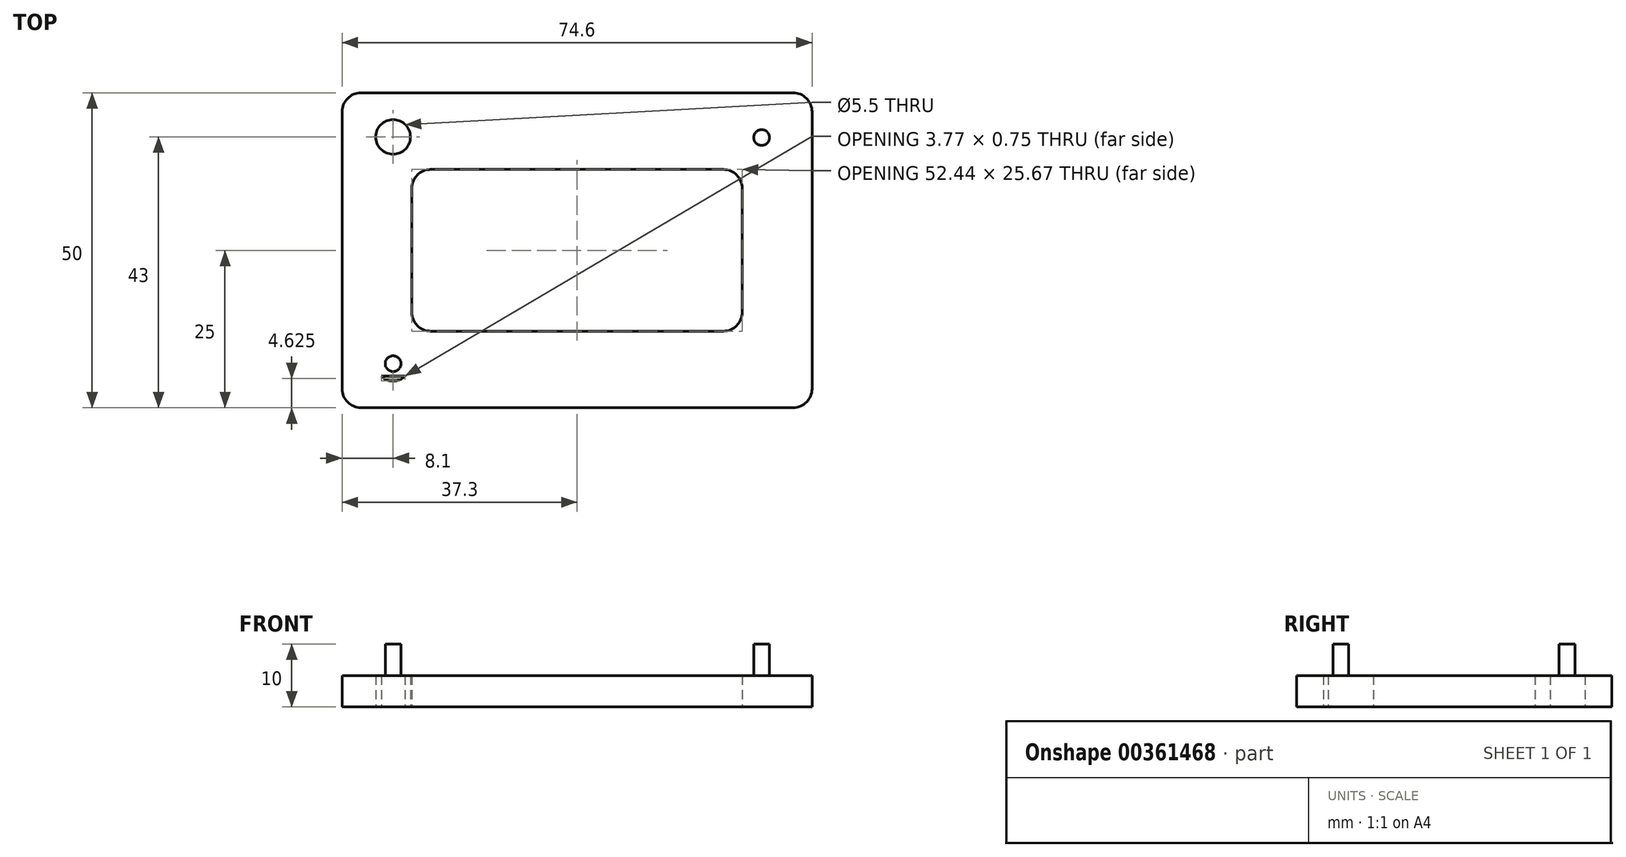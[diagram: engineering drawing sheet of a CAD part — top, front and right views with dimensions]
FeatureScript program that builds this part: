
annotation { "Feature Type Name" : "Feature", "Feature Type Description" : "" }
export const myFeature = defineFeature(function(context is Context, id is Id, definition is map)
    precondition{}
    {
        {
            var Q0;
            Q0=qCreatedBy(makeId("Top.planeOp"),FACE);
            var sketch = newSketch(context, id + "F0", { "sketchPlane" : qUnion([Q0])});
            skLineSegment(sketch, "E0.bottom", {"start": v(-32.3, 20) * mm, "end": v(32.3, 20) * mm});
            skLineSegment(sketch, "E0.top", {"start": v(-32.3, -20) * mm, "end": v(32.3, -20) * mm});
            skLineSegment(sketch, "E0.left", {"start": v(-32.3, 20) * mm, "end": v(-32.3, -20) * mm});
            skLineSegment(sketch, "E0.right", {"start": v(32.3, 20) * mm, "end": v(32.3, -20) * mm});
            skPoint(sketch, "E0.middle", {"position": v(0, 0) * mm});
            skCircle(sketch, "E1", {"center": v(29.3, 17.9) * mm, "radius": 1.25 * mm});
            skCircle(sketch, "E2", {"center": v(-29.2, -18) * mm, "radius": 1.25 * mm});
            skLineSegment(sketch, "E3.0", {"start": v(-37.3, 25) * mm, "end": v(37.3, 25) * mm});
            skLineSegment(sketch, "E3.1", {"start": v(-37.3, 25) * mm, "end": v(-37.3, -25) * mm});
            skLineSegment(sketch, "E3.2", {"start": v(-37.3, -25) * mm, "end": v(37.3, -25) * mm});
            skLineSegment(sketch, "E3.3", {"start": v(37.3, 25) * mm, "end": v(37.3, -25) * mm});
            skCircle(sketch, "E4.0", {"center": v(29.3, 17.9) * mm, "radius": 2.75 * mm});
            skCircle(sketch, "E5.0", {"center": v(-29.2, -18) * mm, "radius": 2.75 * mm});
            skLineSegment(sketch, "E6.bottom", {"start": v(-26.22, 12.84) * mm, "end": v(26.22, 12.84) * mm});
            skLineSegment(sketch, "E6.top", {"start": v(-26.22, -12.84) * mm, "end": v(26.22, -12.84) * mm});
            skLineSegment(sketch, "E6.left", {"start": v(-26.22, 12.84) * mm, "end": v(-26.22, -12.84) * mm});
            skLineSegment(sketch, "E6.right", {"start": v(26.22, 12.84) * mm, "end": v(26.22, -12.84) * mm});
            skCircle(sketch, "E7.MirrorC", {"center": v(-29.2, 18) * mm, "radius": 2.75 * mm});
            skCircle(sketch, "E8.MirrorC", {"center": v(29.3, -17.9) * mm, "radius": 2.75 * mm});
            skSolve(sketch);
        }
        {
            var Q0;
            Q0=makeQuery(id+"F0.imprint","IMPRINT",FACE,{"disambiguationData":[TD([[makeQuery(id+"F0.imprint","IMPRINT",EDGE,{"derivedFrom":sQuery(id+"F0.wireOp",EDGE,"E0.bottom")}),1.0]])]});
            var Q1;
            Q1=makeQuery(id+"F0.imprint","IMPRINT",FACE,{"disambiguationData":[TD([[makeQuery(id+"F0.imprint","IMPRINT",EDGE,{"derivedFrom":sQuery(id+"F0.wireOp",EDGE,"E0.bottom")}),-1.0]])]});
            var Q2;
            Q2=makeQuery(id+"F0.imprint","IMPRINT",FACE,{"disambiguationData":[TD([[makeQuery(id+"F0.imprint","IMPRINT",EDGE,{"derivedFrom":sQuery(id+"F0.wireOp",EDGE,"E2")}),1.0]])]});
            var Q3;
            Q3=makeQuery(id+"F0.imprint","IMPRINT",FACE,{"disambiguationData":[TD([[makeQuery(id+"F0.imprint","IMPRINT",EDGE,{"derivedFrom":sQuery(id+"F0.wireOp",EDGE,"E1")}),1.0]])]});
            var Q4;
            Q4=makeQuery(id+"F0.imprint","IMPRINT",FACE,{"disambiguationData":[TD([[makeQuery(id+"F0.imprint","IMPRINT",EDGE,{"derivedFrom":sQuery(id+"F0.wireOp",EDGE,"E1")}),-1.0]])]});
            var Q5;
            Q5=makeQuery(id+"F0.imprint","IMPRINT",FACE,{"disambiguationData":[TD([[makeQuery(id+"F0.imprint","IMPRINT",EDGE,{"derivedFrom":sQuery(id+"F0.wireOp",EDGE,"E2")}),-1.0]])]});
            var Q6;
            {var subQ1=sQuery(id+"F0.wireOp",EDGE,"E0.left");Q6=makeQuery(id+"F0.imprint","IMPRINT",FACE,{"disambiguationData":[TD([[makeQuery(id+"F0.imprint","IMPRINT",EDGE,{"derivedFrom":subQ1}),-1.0]])]});}
            var Q7;
            {var subQ0=sQuery(id+"F0.wireOp",EDGE,"E5.0");var subQ1=sQuery(id+"F0.wireOp",EDGE,"E0.top");var subQ2=makeQuery(id+"F0.imprint","INTERSECT",VERTEX,{"disambiguationData":[OD(0.0)],"derivedFrom":[subQ1,subQ0]});Q7=makeQuery(id+"F0.imprint","IMPRINT",FACE,{"disambiguationData":[TD([[makeQuery(id+"F0.imprint","IMPRINT",EDGE,{"disambiguationData":[TD([[subQ2,-1.0]])],"derivedFrom":subQ1}),-1.0]])]});}
            extrude(context, id + "F1", {"entities" : qUnion([Q0, Q1, Q2, Q3, Q4, Q5, Q6, Q7]), "depth" : 2 * mm});
        }
        {
            var Q0;
            {var subQ0=sQuery(id+"F0.wireOp",EDGE,"E4.0");var subQ1=sQuery(id+"F0.wireOp",EDGE,"E0.bottom");var subQ2=makeQuery(id+"F0.imprint","INTERSECT",VERTEX,{"disambiguationData":[OD(0.0)],"derivedFrom":[subQ1,subQ0]});Q0=makeQuery(id+"F0.imprint","IMPRINT",FACE,{"disambiguationData":[TD([[makeQuery(id+"F0.imprint","IMPRINT",EDGE,{"disambiguationData":[TD([[subQ2,-1.0]])],"derivedFrom":subQ1}),1.0]])]});}
            var Q1;
            Q1=makeQuery(id+"F0.imprint","IMPRINT",FACE,{"disambiguationData":[TD([[makeQuery(id+"F0.imprint","IMPRINT",EDGE,{"derivedFrom":sQuery(id+"F0.wireOp",EDGE,"E1")}),-1.0]])]});
            var Q2;
            Q2=makeQuery(id+"F0.imprint","IMPRINT",FACE,{"disambiguationData":[TD([[makeQuery(id+"F0.imprint","IMPRINT",EDGE,{"derivedFrom":sQuery(id+"F0.wireOp",EDGE,"E1")}),1.0]])]});
            var Q3;
            Q3=makeQuery(id+"F0.imprint","IMPRINT",FACE,{"disambiguationData":[TD([[makeQuery(id+"F0.imprint","IMPRINT",EDGE,{"derivedFrom":sQuery(id+"F0.wireOp",EDGE,"E2")}),-1.0]])]});
            var Q4;
            Q4=makeQuery(id+"F0.imprint","IMPRINT",FACE,{"disambiguationData":[TD([[makeQuery(id+"F0.imprint","IMPRINT",EDGE,{"derivedFrom":sQuery(id+"F0.wireOp",EDGE,"E2")}),1.0]])]});
            var Q5;
            {var subQ0=sQuery(id+"F0.wireOp",EDGE,"E5.0");var subQ1=sQuery(id+"F0.wireOp",EDGE,"E0.top");var subQ2=makeQuery(id+"F0.imprint","INTERSECT",VERTEX,{"disambiguationData":[OD(0.0)],"derivedFrom":[subQ1,subQ0]});Q5=makeQuery(id+"F0.imprint","IMPRINT",FACE,{"disambiguationData":[TD([[makeQuery(id+"F0.imprint","IMPRINT",EDGE,{"disambiguationData":[TD([[subQ2,-1.0]])],"derivedFrom":subQ1}),-1.0]])]});}
            var Q6;
            {var subQ0=sQuery(id+"F0.wireOp",EDGE,"E7.MirrorC");var subQ1=sQuery(id+"F0.wireOp",EDGE,"E0.bottom");var subQ2=makeQuery(id+"F0.imprint","INTERSECT",VERTEX,{"disambiguationData":[OD(0.0)],"derivedFrom":[subQ1,subQ0]});Q6=makeQuery(id+"F0.imprint","IMPRINT",FACE,{"disambiguationData":[TD([[makeQuery(id+"F0.imprint","IMPRINT",EDGE,{"disambiguationData":[TD([[subQ2,-1.0]])],"derivedFrom":subQ1}),-1.0]])]});}
            var Q7;
            {var subQ0=sQuery(id+"F0.wireOp",EDGE,"E7.MirrorC");var subQ1=sQuery(id+"F0.wireOp",EDGE,"E0.bottom");var subQ2=makeQuery(id+"F0.imprint","INTERSECT",VERTEX,{"disambiguationData":[OD(0.0)],"derivedFrom":[subQ1,subQ0]});Q7=makeQuery(id+"F0.imprint","IMPRINT",FACE,{"disambiguationData":[TD([[makeQuery(id+"F0.imprint","IMPRINT",EDGE,{"disambiguationData":[TD([[subQ2,-1.0]])],"derivedFrom":subQ1}),1.0]])]});}
            var Q8;
            {var subQ0=sQuery(id+"F0.wireOp",EDGE,"E8.MirrorC");var subQ1=sQuery(id+"F0.wireOp",EDGE,"E0.top");var subQ2=makeQuery(id+"F0.imprint","INTERSECT",VERTEX,{"disambiguationData":[OD(0.0)],"derivedFrom":[subQ1,subQ0]});Q8=makeQuery(id+"F0.imprint","IMPRINT",FACE,{"disambiguationData":[TD([[makeQuery(id+"F0.imprint","IMPRINT",EDGE,{"disambiguationData":[TD([[subQ2,-1.0]])],"derivedFrom":subQ1}),1.0]])]});}
            var Q9;
            {var subQ0=sQuery(id+"F0.wireOp",EDGE,"E8.MirrorC");var subQ1=sQuery(id+"F0.wireOp",EDGE,"E0.top");var subQ2=makeQuery(id+"F0.imprint","INTERSECT",VERTEX,{"disambiguationData":[OD(0.0)],"derivedFrom":[subQ1,subQ0]});Q9=makeQuery(id+"F0.imprint","IMPRINT",FACE,{"disambiguationData":[TD([[makeQuery(id+"F0.imprint","IMPRINT",EDGE,{"disambiguationData":[TD([[subQ2,-1.0]])],"derivedFrom":subQ1}),-1.0]])]});}
            extrude(context, id + "F2", {"entities" : qUnion([Q0, Q1, Q2, Q3, Q4, Q5, Q6, Q7, Q8, Q9]), "operationType" : NewBodyOperationType.ADD, "depth" : 5 * mm});
        }
        {
            var Q0;
            Q0=makeQuery(id+"F0.imprint","IMPRINT",FACE,{"disambiguationData":[TD([[makeQuery(id+"F0.imprint","IMPRINT",EDGE,{"derivedFrom":sQuery(id+"F0.wireOp",EDGE,"E1")}),1.0]])]});
            var Q1;
            Q1=makeQuery(id+"F0.imprint","IMPRINT",FACE,{"disambiguationData":[TD([[makeQuery(id+"F0.imprint","IMPRINT",EDGE,{"derivedFrom":sQuery(id+"F0.wireOp",EDGE,"E2")}),1.0]])]});
            extrude(context, id + "F3", {"entities" : qUnion([Q0, Q1]), "operationType" : NewBodyOperationType.ADD, "depth" : 10 * mm});
        }
        {
            var Q0;
            Q0=makeQuery(id+"F1.opExtrude","SWEPT_EDGE",EDGE,{"disambiguationData":[OSD([sQuery(id+"F0.wireOp",EDGE,"E3.0"),sQuery(id+"F0.wireOp",EDGE,"E3.3")])]});
            var Q1;
            Q1=makeQuery(id+"F1.opExtrude","SWEPT_EDGE",EDGE,{"disambiguationData":[OSD([sQuery(id+"F0.wireOp",EDGE,"E3.2"),sQuery(id+"F0.wireOp",EDGE,"E3.3")])]});
            var Q2;
            Q2=makeQuery(id+"F1.opExtrude","SWEPT_EDGE",EDGE,{"disambiguationData":[OSD([sQuery(id+"F0.wireOp",EDGE,"E3.1"),sQuery(id+"F0.wireOp",EDGE,"E3.2")])]});
            var Q3;
            Q3=makeQuery(id+"F1.opExtrude","SWEPT_EDGE",EDGE,{"disambiguationData":[OSD([sQuery(id+"F0.wireOp",EDGE,"E3.0"),sQuery(id+"F0.wireOp",EDGE,"E3.1")])]});
            fillet(context, id + "F4", {"entities" : qUnion([Q0, Q1, Q2, Q3]), "radius" : 3 * mm, "tangentPropagation" : true, "allowEdgeOverflow" : false});
        }
        {
            var Q0;
            Q0=makeQuery(id+"F1.opExtrude","SWEPT_EDGE",EDGE,{"disambiguationData":[OSD([sQuery(id+"F0.wireOp",EDGE,"E6.bottom"),sQuery(id+"F0.wireOp",EDGE,"E6.left")])]});
            var Q1;
            Q1=makeQuery(id+"F1.opExtrude","SWEPT_EDGE",EDGE,{"disambiguationData":[OSD([sQuery(id+"F0.wireOp",EDGE,"E6.bottom"),sQuery(id+"F0.wireOp",EDGE,"E6.right")])]});
            var Q2;
            Q2=makeQuery(id+"F1.opExtrude","SWEPT_EDGE",EDGE,{"disambiguationData":[OSD([sQuery(id+"F0.wireOp",EDGE,"E6.top"),sQuery(id+"F0.wireOp",EDGE,"E6.right")])]});
            var Q3;
            Q3=makeQuery(id+"F1.opExtrude","SWEPT_EDGE",EDGE,{"disambiguationData":[OSD([sQuery(id+"F0.wireOp",EDGE,"E6.top"),sQuery(id+"F0.wireOp",EDGE,"E6.left")])]});
            fillet(context, id + "F5", {"entities" : qUnion([Q0, Q1, Q2, Q3]), "radius" : 3 * mm, "tangentPropagation" : true, "allowEdgeOverflow" : false});
        }
    });
